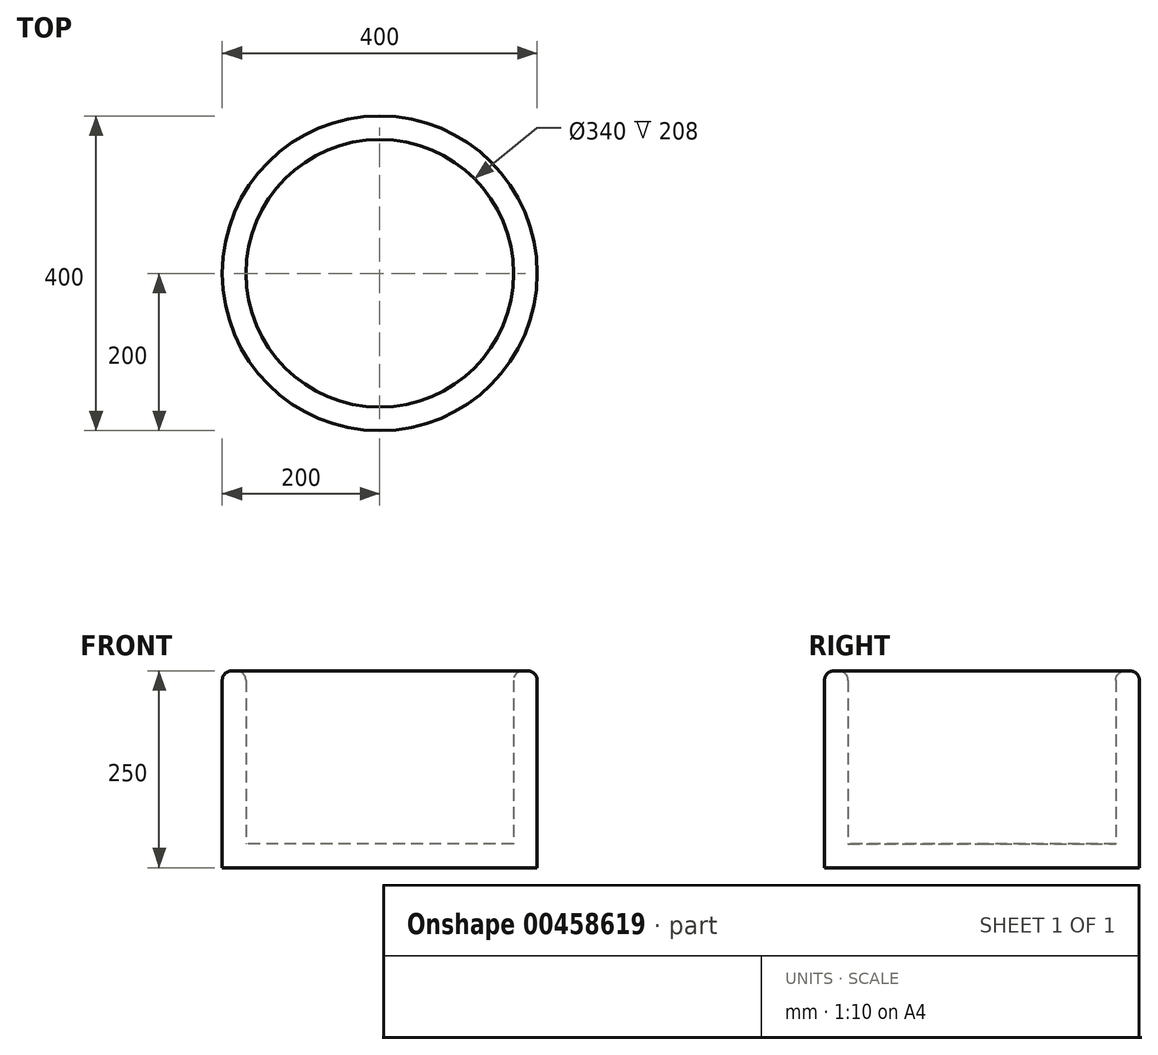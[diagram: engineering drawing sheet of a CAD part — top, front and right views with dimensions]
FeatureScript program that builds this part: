
annotation { "Feature Type Name" : "Feature", "Feature Type Description" : "" }
export const myFeature = defineFeature(function(context is Context, id is Id, definition is map)
    precondition{}
    {
        {
            var Q0;
            Q0=qCreatedBy(makeId("Top.planeOp"),FACE);
            var sketch = newSketch(context, id + "F0", { "sketchPlane" : qUnion([Q0])});
            skCircle(sketch, "E0", {"center": v(0, 0) * mm, "radius": 200 * mm});
            skCircle(sketch, "E1.0", {"center": v(0, 0) * mm, "radius": 170 * mm});
            skSolve(sketch);
        }
        {
            var Q0;
            Q0 = qSketchRegion(id + "F0", true);
            extrude(context, id + "F1", {"entities" : qUnion([Q0]), "depth" : 250 * mm});
        }
        {
            var Q0;
            Q0=qCreatedBy(makeId("Top.planeOp"),FACE);
            var sketch = newSketch(context, id + "F2", { "sketchPlane" : qUnion([Q0])});
            skCircle(sketch, "E2.0", {"center": v(0, 0) * mm, "radius": 170 * mm});
            skSolve(sketch);
        }
        {
            var Q0;
            Q0=makeQuery(id+"F2.imprint","IMPRINT",FACE,{"disambiguationData":[TD([[makeQuery(id+"F2.imprint","IMPRINT",EDGE,{"derivedFrom":sQuery(id+"F2.wireOp",EDGE,"E2.0")}),1.0]])]});
            extrude(context, id + "F3", {"entities" : qUnion([Q0]), "operationType" : NewBodyOperationType.ADD, "depth" : 30 * mm});
        }
        {
            var Q0;
            Q0=makeQuery(id+"F1.opExtrude","CAP_EDGE",EDGE,{"disambiguationData":[OSD([sQuery(id+"F0.wireOp",EDGE,"E1.0")])],"isStart":false});
            var Q1;
            Q1=makeQuery(id+"F1.opExtrude","CAP_EDGE",EDGE,{"disambiguationData":[OSD([sQuery(id+"F0.wireOp",EDGE,"E0")])],"isStart":false});
            fillet(context, id + "F4", {"entities" : qUnion([Q0, Q1]), "radius" : 12 * mm, "tangentPropagation" : true, "allowEdgeOverflow" : false});
        }
    });
